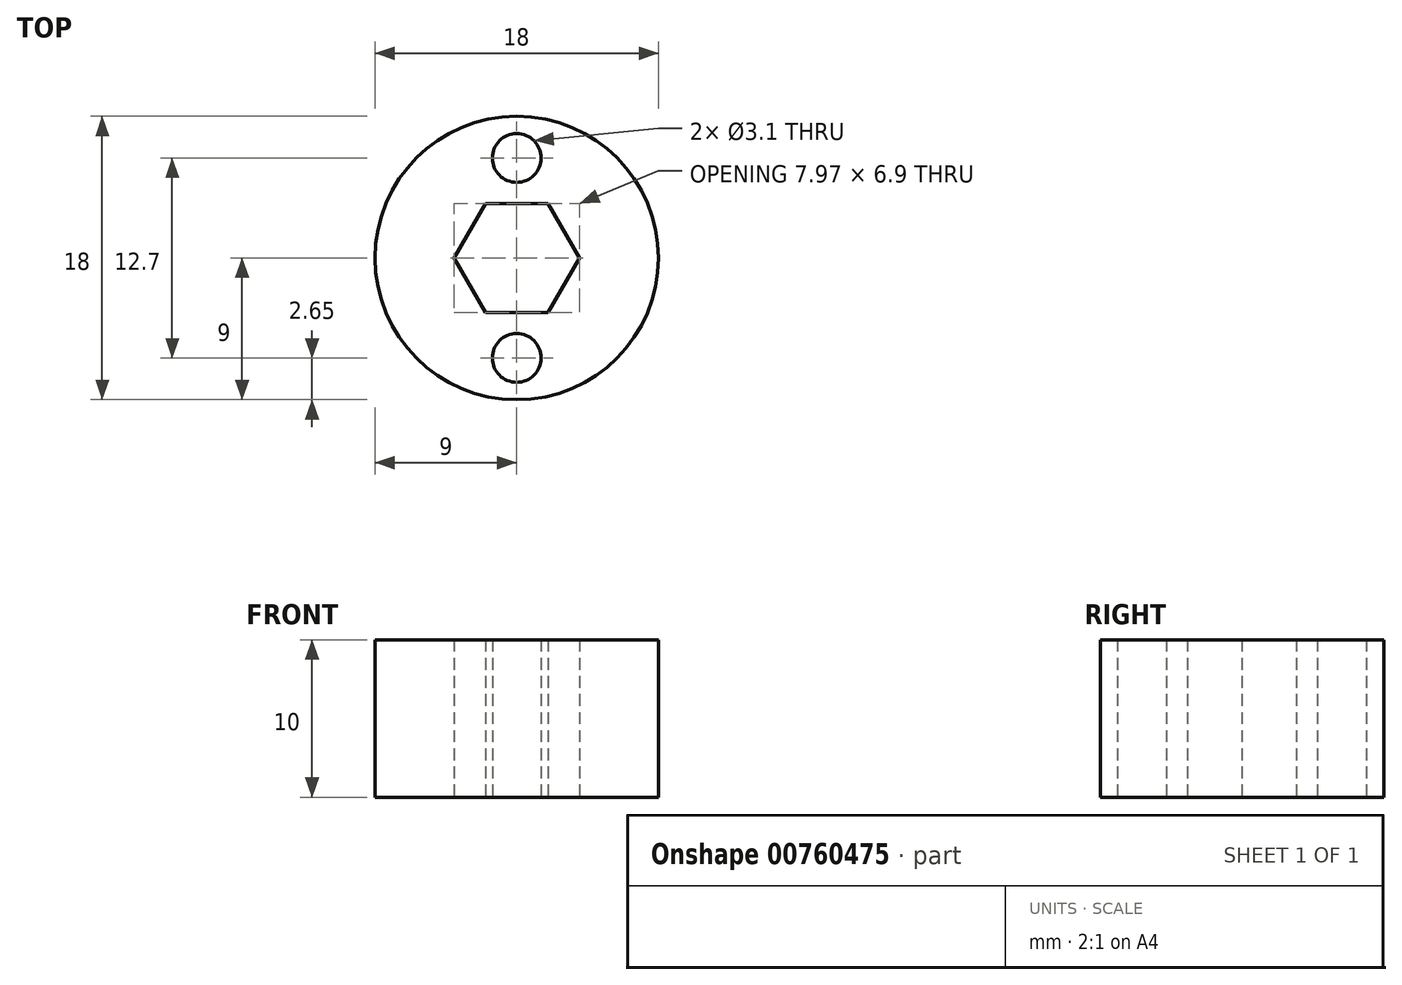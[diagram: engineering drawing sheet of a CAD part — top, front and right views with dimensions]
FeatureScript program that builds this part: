
annotation { "Feature Type Name" : "Feature", "Feature Type Description" : "" }
export const myFeature = defineFeature(function(context is Context, id is Id, definition is map)
    precondition{}
    {
        {
            var Q0;
            Q0=qCreatedBy(makeId("Top.planeOp"),FACE);
            var sketch = newSketch(context, id + "F0", { "sketchPlane" : qUnion([Q0])});
            skCircle(sketch, "E0", {"center": v(0, 0) * mm, "radius": 9 * mm});
            skCircle(sketch, "E1", {"center": v(6.35, 0) * mm, "radius": 1.55 * mm});
            skCircle(sketch, "E2.1.0", {"center": v(0, 6.35) * mm, "radius": 1.55 * mm});
            skCircle(sketch, "E2.2.0", {"center": v(-6.35, 0) * mm, "radius": 1.55 * mm});
            skCircle(sketch, "E2.3.0", {"center": v(0, -6.35) * mm, "radius": 1.55 * mm});
            skCircle(sketch, "E3.cCircle", {"center": v(0, 0) * mm, "radius": 3.45 * mm, "construction": true});
            skLineSegment(sketch, "E3.0", {"start": v(-2, 3.45) * mm, "end": v(2, 3.45) * mm});
            skLineSegment(sketch, "E3.1", {"start": v(2, 3.45) * mm, "end": v(3.98, 0) * mm});
            skLineSegment(sketch, "E3.2", {"start": v(3.98, 0) * mm, "end": v(2, -3.45) * mm});
            skLineSegment(sketch, "E3.3", {"start": v(2, -3.45) * mm, "end": v(-2, -3.45) * mm});
            skLineSegment(sketch, "E3.4", {"start": v(-2, -3.45) * mm, "end": v(-3.98, 0) * mm});
            skLineSegment(sketch, "E3.5", {"start": v(-3.98, 0) * mm, "end": v(-2, 3.45) * mm});
            skPoint(sketch, "E3.0.midPoint", {"position": v(0, 3.45) * mm});
            skSolve(sketch);
        }
        {
            var Q0;
            Q0=makeQuery(id+"F0.imprint","IMPRINT",FACE,{"disambiguationData":[TD([[makeQuery(id+"F0.imprint","IMPRINT",EDGE,{"derivedFrom":sQuery(id+"F0.wireOp",EDGE,"E0")}),1.0]])]});
            var Q1;
            Q1=makeQuery(id+"F0.imprint","IMPRINT",FACE,{"disambiguationData":[TD([[makeQuery(id+"F0.imprint","IMPRINT",EDGE,{"derivedFrom":sQuery(id+"F0.wireOp",EDGE,"E2.2.0")}),1.0]])]});
            var Q2;
            Q2=makeQuery(id+"F0.imprint","IMPRINT",FACE,{"disambiguationData":[TD([[makeQuery(id+"F0.imprint","IMPRINT",EDGE,{"derivedFrom":sQuery(id+"F0.wireOp",EDGE,"E1")}),1.0]])]});
            extrude(context, id + "F1", {"entities" : qUnion([Q0, Q1, Q2]), "depth" : 10 * mm, "offsetDistance" : 25 * mm});
        }
    });
